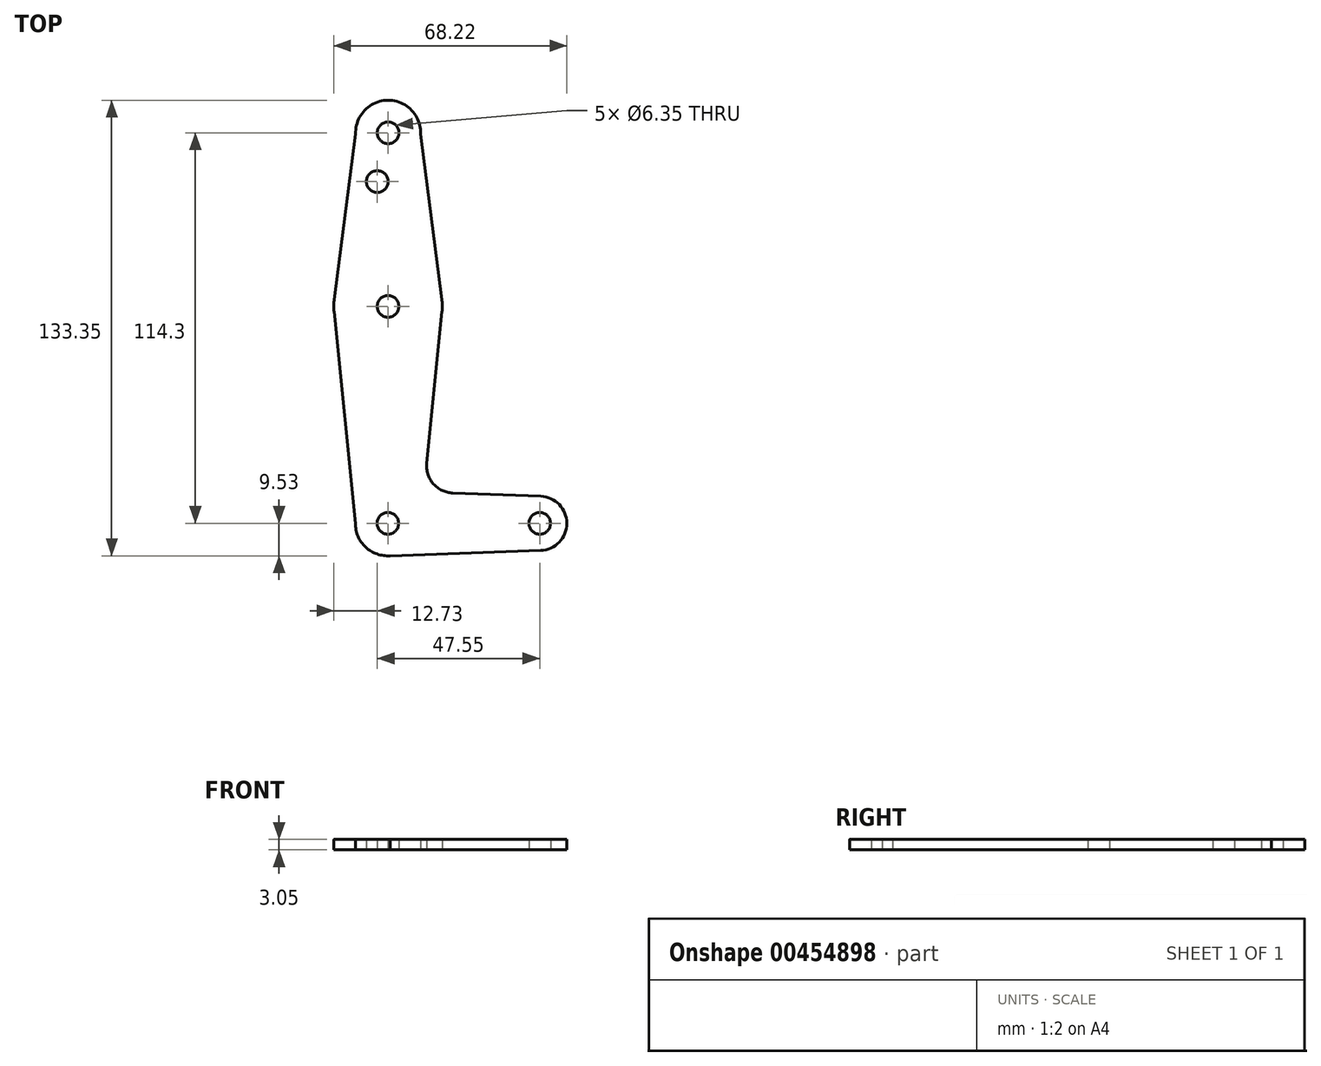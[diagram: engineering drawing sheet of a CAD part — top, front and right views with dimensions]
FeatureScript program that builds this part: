
annotation { "Feature Type Name" : "Feature", "Feature Type Description" : "" }
export const myFeature = defineFeature(function(context is Context, id is Id, definition is map)
    precondition{}
    {
        {
            var Q0;
            Q0=qCreatedBy(makeId("Top.planeOp"),FACE);
            var sketch = newSketch(context, id + "F0", { "sketchPlane" : qUnion([Q0])});
            skLineSegment(sketch, "E0", {"start": v(0, 0) * mm, "end": v(44.45, 0) * mm, "construction": true});
            skCircle(sketch, "E1", {"center": v(0.09, 114.3) * mm, "radius": 9.53 * mm});
            skCircle(sketch, "E2", {"center": v(0, 0) * mm, "radius": 9.53 * mm});
            skCircle(sketch, "E3", {"center": v(44.45, 0) * mm, "radius": 7.94 * mm});
            skCircle(sketch, "E4", {"center": v(0.05, 63.5) * mm, "radius": 15.88 * mm});
            skLineSegment(sketch, "E5", {"start": v(0.09, 114.3) * mm, "end": v(0, 0) * mm, "construction": true});
            skLineSegment(sketch, "E6", {"start": v(0, -9.53) * mm, "end": v(44.73, -7.93) * mm});
            skLineSegment(sketch, "E7", {"start": v(19.02, 8.85) * mm, "end": v(44.73, 7.93) * mm});
            skLineSegment(sketch, "E8", {"start": v(11.39, 17.59) * mm, "end": v(15.84, 61.91) * mm});
            skLineSegment(sketch, "E9", {"start": v(-9.52, 0) * mm, "end": v(-15.75, 61.91) * mm});
            skCircle(sketch, "E10", {"center": v(0.09, 114.3) * mm, "radius": 3.18 * mm});
            skCircle(sketch, "E11", {"center": v(0.05, 63.5) * mm, "radius": 3.18 * mm});
            skCircle(sketch, "E12", {"center": v(0, 0) * mm, "radius": 3.18 * mm});
            skCircle(sketch, "E13", {"center": v(44.45, 0) * mm, "radius": 3.18 * mm});
            skCircle(sketch, "E14", {"center": v(-3.1, 100.03) * mm, "radius": 3.18 * mm});
            skArc(sketch, "E15.filletArc", {"start": v(11.39, 17.59) * mm, "mid": v(13.3, 11.57) * mm, "end": v(19.02, 8.85) * mm});
            skLineSegment(sketch, "E16", {"start": v(9.6, 113.93) * mm, "end": v(15.8, 65.51) * mm});
            skLineSegment(sketch, "E17", {"start": v(-9.43, 113.93) * mm, "end": v(-15.7, 65.54) * mm});
            skSolve(sketch);
        }
        {
            var Q0;
            Q0 = qSketchRegion(id + "F0", true);
            extrude(context, id + "F1", {"entities" : qUnion([Q0]), "depth" : 3.05 * mm});
        }
    });
